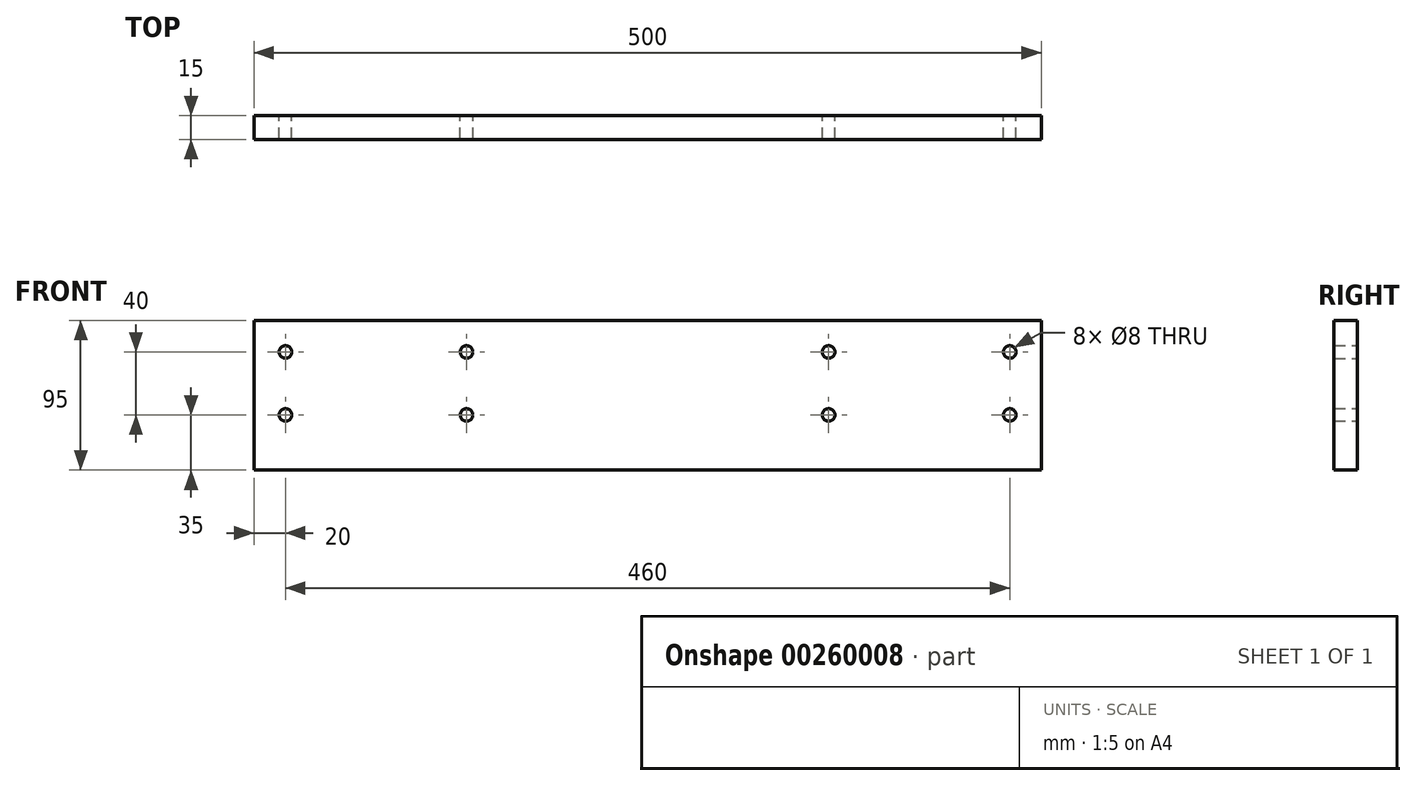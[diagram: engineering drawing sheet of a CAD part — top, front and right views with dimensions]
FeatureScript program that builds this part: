
annotation { "Feature Type Name" : "Feature", "Feature Type Description" : "" }
export const myFeature = defineFeature(function(context is Context, id is Id, definition is map)
    precondition{}
    {
        {
            var Q0;
            Q0=qCreatedBy(makeId("Front.planeOp"),FACE);
            var sketch = newSketch(context, id + "F0", { "sketchPlane" : qUnion([Q0]), "disableImprinting" : false});
            skLineSegment(sketch, "E0", {"start": v(0, 0) * mm, "end": v(0, 95) * mm});
            skLineSegment(sketch, "E1", {"start": v(0, 95) * mm, "end": v(500, 95) * mm});
            skLineSegment(sketch, "E2", {"start": v(500, 95) * mm, "end": v(500, 0) * mm});
            skCircle(sketch, "E3", {"center": v(135, 75) * mm, "radius": 4 * mm});
            skCircle(sketch, "E4", {"center": v(135, 35) * mm, "radius": 4 * mm});
            skLineSegment(sketch, "E5", {"start": v(500, 0) * mm, "end": v(0, 0) * mm});
            skLineSegment(sketch, "E6", {"start": v(250, 95) * mm, "end": v(250, 0) * mm, "construction": true});
            skCircle(sketch, "E7.MirrorC", {"center": v(365, 75) * mm, "radius": 4 * mm});
            skCircle(sketch, "E8.MirrorC", {"center": v(365, 35) * mm, "radius": 4 * mm});
            skCircle(sketch, "E9", {"center": v(20, 35) * mm, "radius": 4 * mm});
            skCircle(sketch, "E10", {"center": v(20, 75) * mm, "radius": 4 * mm});
            skCircle(sketch, "E11.MirrorC", {"center": v(480, 75) * mm, "radius": 4 * mm});
            skCircle(sketch, "E12.MirrorC", {"center": v(480, 35) * mm, "radius": 4 * mm});
            skSolve(sketch);
        }
        {
            var Q0;
            Q0=makeQuery(id+"F0.imprint","IMPRINT",FACE,{"disambiguationData":[TD([[makeQuery(id+"F0.imprint","IMPRINT",EDGE,{"derivedFrom":sQuery(id+"F0.wireOp",EDGE,"E0")}),-1.0]])]});
            extrude(context, id + "F1", {"entities" : qUnion([Q0]), "flatOperationType" : FlatOperationType.REMOVE, "depth" : 15 * mm, "offsetDistance" : 25 * mm, "domain" : OperationDomain.MODEL});
        }
    });
